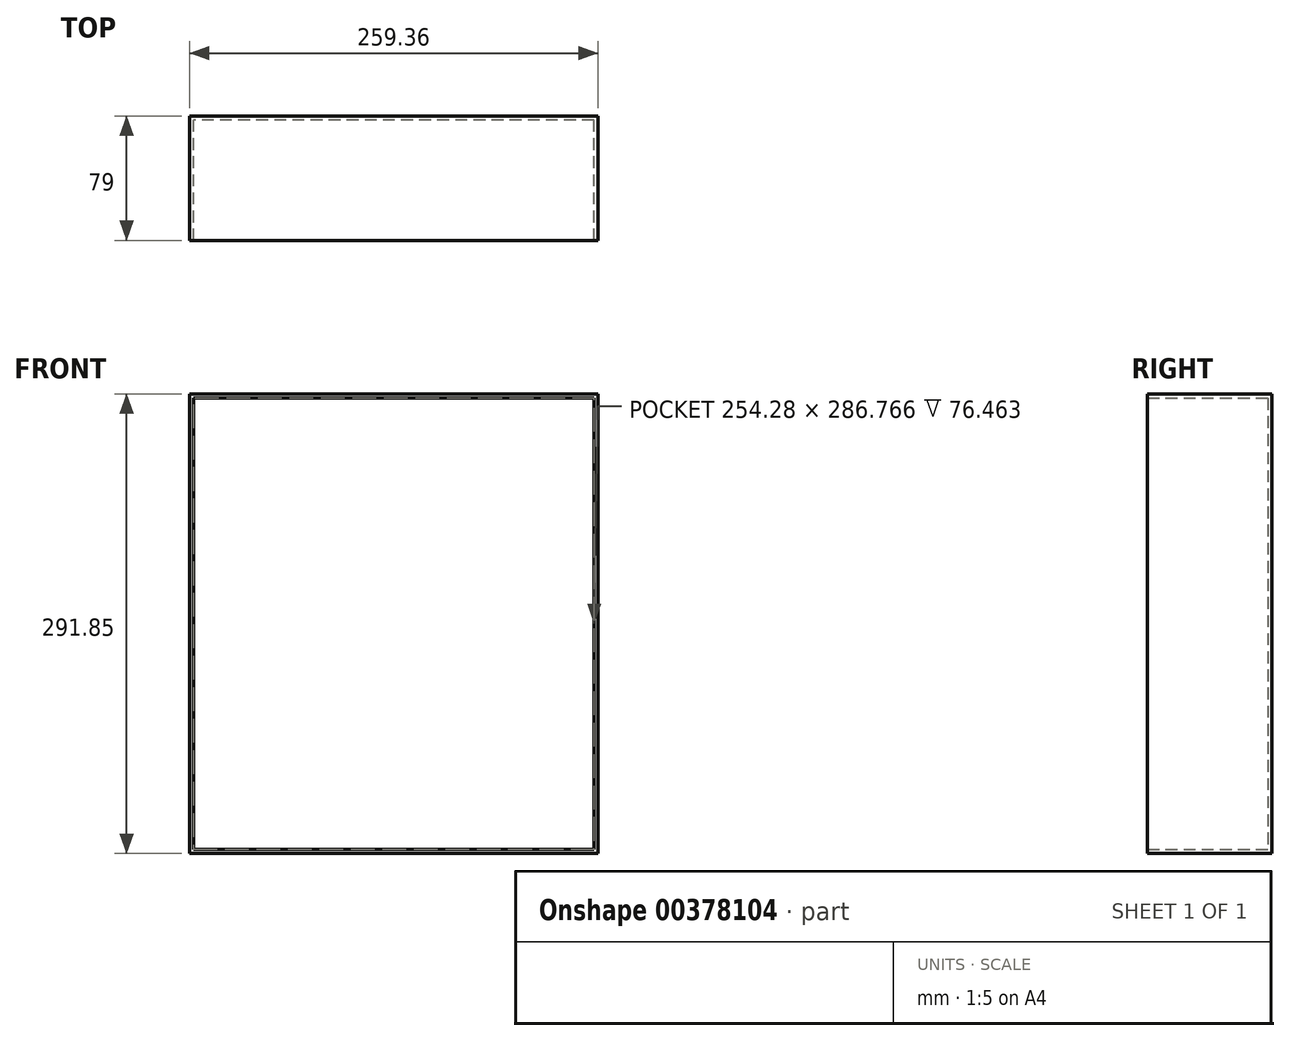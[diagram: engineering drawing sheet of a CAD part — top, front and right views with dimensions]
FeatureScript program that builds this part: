
annotation { "Feature Type Name" : "Feature", "Feature Type Description" : "" }
export const myFeature = defineFeature(function(context is Context, id is Id, definition is map)
    precondition{}
    {
        {
            var Q0;
            Q0=qCreatedBy(makeId("Top.planeOp"),FACE);
            var sketch = newSketch(context, id + "F0", { "sketchPlane" : qUnion([Q0])});
            skLineSegment(sketch, "E0.bottom", {"start": v(-5.08, 26.26) * mm, "end": v(-81.3, 26.26) * mm});
            skLineSegment(sketch, "E0.top", {"start": v(-5.08, 51.66) * mm, "end": v(-81.3, 51.66) * mm});
            skLineSegment(sketch, "E0.left", {"start": v(-5.08, 26.26) * mm, "end": v(-5.08, 51.66) * mm});
            skLineSegment(sketch, "E0.right", {"start": v(-81.3, 26.26) * mm, "end": v(-81.3, 51.66) * mm});
            skPoint(sketch, "E0.middle", {"position": v(-43.2, 38.96) * mm});
            skSolve(sketch);
        }
        {
            var Q0;
            Q0=makeQuery(id+"F0.imprint","IMPRINT",FACE,{"disambiguationData":[TD([[makeQuery(id+"F0.imprint","IMPRINT",EDGE,{"derivedFrom":sQuery(id+"F0.wireOp",EDGE,"E0.bottom")}),-1.0]])]});
            extrude(context, id + "F1", {"entities" : qUnion([Q0]), "depth" : 113.8 * mm});
        }
        {
            var Q0;
            Q0=makeQuery(id+"F1.opExtrude","SWEPT_FACE",FACE,{"disambiguationData":[OSD([sQuery(id+"F0.wireOp",EDGE,"E0.left")])]});
            extrude(context, id + "F2", {"entities" : qUnion([Q0]), "operationType" : NewBodyOperationType.ADD, "depth" : 183.13 * mm});
        }
        {
            var Q0;
            {var subQ0=sQuery(id+"F0.wireOp",EDGE,"E0.left");Q0=makeQuery(id+"F2.boolean.opBoolean","MERGE",FACE,{"derivedFrom":[makeQuery(id+"F1.opExtrude","CAP_FACE",FACE,{"disambiguationData":[OSD([sQuery(id+"F0.wireOp",EDGE,"E0.bottom"),sQuery(id+"F0.wireOp",EDGE,"E0.top"),subQ0,sQuery(id+"F0.wireOp",EDGE,"E0.right")])],"isStart":false}),makeQuery(id+"F2.opExtrude","SWEPT_FACE",FACE,{"disambiguationData":[OSD([subQ0]),TDD([makeQuery(id+"F1.opExtrude","CAP_EDGE",EDGE,{"disambiguationData":[OSD([subQ0])],"isStart":false})])]})]});}
            extrude(context, id + "F3", {"entities" : qUnion([Q0]), "operationType" : NewBodyOperationType.ADD, "depth" : 178.05 * mm});
        }
        {
            var Q0;
            {var subQ0=sQuery(id+"F0.wireOp",EDGE,"E0.left");var subQ1=sQuery(id+"F0.wireOp",EDGE,"E0.bottom");Q0=makeQuery(id+"F3.boolean.opBoolean","MERGE",FACE,{"derivedFrom":[makeQuery(id+"F2.boolean.opBoolean","MERGE",FACE,{"derivedFrom":[makeQuery(id+"F1.opExtrude","SWEPT_FACE",FACE,{"disambiguationData":[OSD([subQ1])]}),makeQuery(id+"F2.opExtrude","SWEPT_FACE",FACE,{"disambiguationData":[OSD([subQ1,subQ0])]})]}),makeQuery(id+"F3.opExtrude","SWEPT_FACE",FACE,{"disambiguationData":[OSD([subQ1,subQ0])]})]});}
            extrude(context, id + "F4", {"entities" : qUnion([Q0]), "operationType" : NewBodyOperationType.ADD, "depth" : 53.6 * mm});
        }
        {
            var Q0;
            Q0=makeQuery(id+"F4.opExtrude","CAP_FACE",FACE,{"disambiguationData":[OSD([sQuery(id+"F0.wireOp",EDGE,"E0.bottom"),sQuery(id+"F0.wireOp",EDGE,"E0.left")])],"isStart":false});
            shell(context, id + "F5", {"entities" : qUnion([Q0]), "thickness" : 2.54 * mm});
        }
    });
